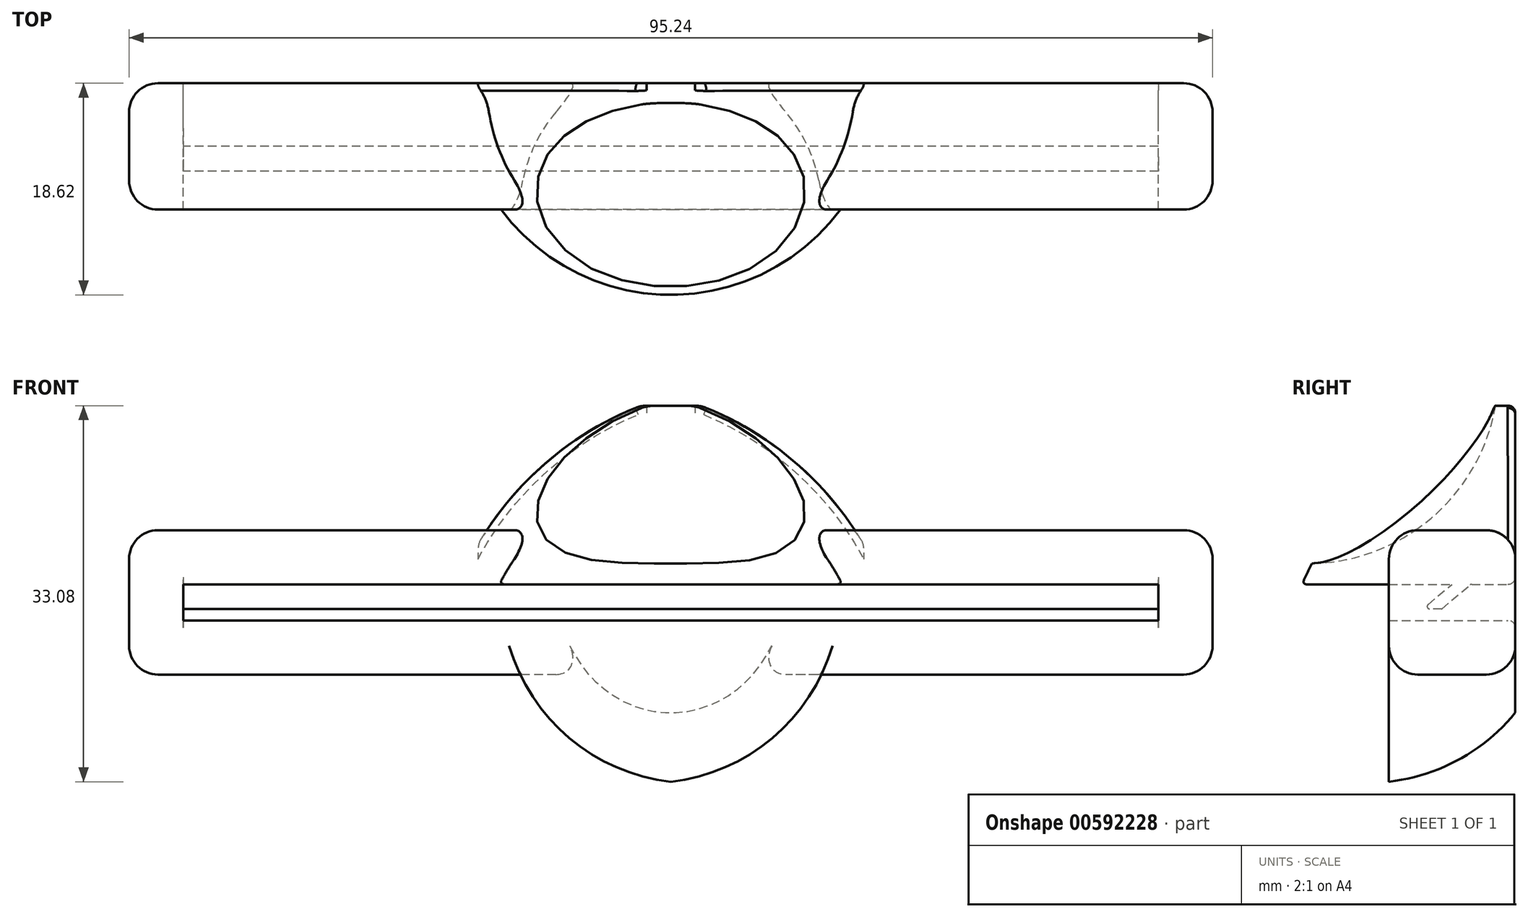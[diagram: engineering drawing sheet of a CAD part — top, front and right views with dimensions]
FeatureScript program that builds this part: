
annotation { "Feature Type Name" : "Feature", "Feature Type Description" : "" }
export const myFeature = defineFeature(function(context is Context, id is Id, definition is map)
    precondition{}
    {
        {
            var Q0;
            Q0=qCreatedBy(makeId("Front.planeOp"),FACE);
            var sketch = newSketch(context, id + "F0", { "sketchPlane" : qUnion([Q0])});
            skLineSegment(sketch, "E0.bottom", {"start": v(42.86, -1.59) * mm, "end": v(-42.86, -1.59) * mm});
            skLineSegment(sketch, "E0.top", {"start": v(42.86, 1.59) * mm, "end": v(-42.86, 1.59) * mm});
            skLineSegment(sketch, "E0.left", {"start": v(42.86, -1.59) * mm, "end": v(42.86, 1.59) * mm});
            skLineSegment(sketch, "E0.right", {"start": v(-42.86, -1.59) * mm, "end": v(-42.86, 1.59) * mm});
            skPoint(sketch, "E0.middle", {"position": v(0, 0) * mm});
            skLineSegment(sketch, "E1.0", {"start": v(47.63, 6.35) * mm, "end": v(-47.62, 6.35) * mm});
            skLineSegment(sketch, "E1.1", {"start": v(47.63, -6.35) * mm, "end": v(47.63, 6.35) * mm});
            skLineSegment(sketch, "E1.2", {"start": v(47.63, -6.35) * mm, "end": v(-47.62, -6.35) * mm});
            skLineSegment(sketch, "E1.3", {"start": v(-47.62, -6.35) * mm, "end": v(-47.62, 6.35) * mm});
            skSolve(sketch);
        }
        {
            var Q0;
            Q0 = qSketchRegion(id + "F0", true);
            extrude(context, id + "F1", {"entities" : qUnion([Q0]), "depth" : 11.1 * mm, "offsetDistance" : 25.4 * mm});
        }
        {
            var Q0;
            Q0=makeQuery(id+"F1.opExtrude","SWEPT_FACE",FACE,{"disambiguationData":[OSD([sQuery(id+"F0.wireOp",EDGE,"E0.right")])]});
            var sketch = newSketch(context, id + "F2", { "sketchPlane" : qUnion([Q0])});
            skLineSegment(sketch, "E2", {"start": v(-5.56, 1.59) * mm, "end": v(-8.12, -0.58) * mm});
            skLineSegment(sketch, "E3", {"start": v(-8.12, -0.58) * mm, "end": v(-6.48, -0.58) * mm});
            skLineSegment(sketch, "E4.0.1", {"start": v(0, 6.35) * mm, "end": v(-11.11, 6.35) * mm});
            skLineSegment(sketch, "E4.0.2", {"start": v(-11.11, 6.35) * mm, "end": v(-11.11, -6.35) * mm});
            skLineSegment(sketch, "E4.0.3", {"start": v(-11.11, -6.35) * mm, "end": v(0, -6.35) * mm});
            skLineSegment(sketch, "E5", {"start": v(-3.9, 1.59) * mm, "end": v(-6.46, -0.57) * mm});
            skPoint(sketch, "E6.visualSharp", {"position": v(-6.47, -0.58) * mm});
            skArc(sketch, "E6.filletArc", {"start": v(-6.48, -0.58) * mm, "mid": v(-6.47, -0.57) * mm, "end": v(-6.46, -0.57) * mm});
            skLineSegment(sketch, "E7", {"start": v(-5.56, 1.59) * mm, "end": v(-3.9, 1.59) * mm});
            skSolve(sketch);
        }
        {
            var Q0;
            Q0 = qSketchRegion(id + "F2", true);
            extrude(context, id + "F3", {"entities" : qUnion([Q0]), "operationType" : NewBodyOperationType.ADD, "endBound" : BoundingType.UP_TO_NEXT, "depth" : 25.4 * mm, "offsetDistance" : 25.4 * mm});
        }
        {
            var Q0;
            Q0=makeQuery(id+"F3.opExtrude","SWEPT_EDGE",EDGE,{"disambiguationData":[OSD([sQuery(id+"F0.wireOp",EDGE,"E0.top"),sQuery(id+"F0.wireOp",EDGE,"E0.right"),sQuery(id+"F2.wireOp",EDGE,"TzPzhfrO-n8Sb-AZqS-cfUP-Q4RwWiP4V3qO"),sQuery(id+"F2.wireOp",EDGE,"DA7K2Kf5-dVk4-9vVa-SaD1-1n64DXrW5RF1")])]});
            fillet(context, id + "F4", {"entities" : qUnion([Q0]), "radius" : 0.22 * mm, "tangentPropagation" : true, "allowEdgeOverflow" : false});
        }
        {
            var Q0;
            Q0=qCreatedBy(makeId("Right.planeOp"),FACE);
            var sketch = newSketch(context, id + "F5", { "sketchPlane" : qUnion([Q0])});
            skLineSegment(sketch, "E8", {"start": v(0, 1.59) * mm, "end": v(0, 17.3) * mm});
            skLineSegment(sketch, "E9.0", {"start": v(-11.11, -6.35) * mm, "end": v(-11.11, 6.35) * mm, "construction": true});
            skPoint(sketch, "E10", {"position": v(-19.34, 0) * mm});
            skPoint(sketch, "E10.positionSnap0", {"position": v(-11.11, 0) * mm});
            skArc(sketch, "E11", {"start": v(-3.2, 17.1) * mm, "mid": v(-12.37, 11) * mm, "end": v(-18.6, 1.9) * mm});
            skLineSegment(sketch, "E12.0", {"start": v(-11.11, 6.35) * mm, "end": v(0, 6.35) * mm, "construction": true});
            skLineSegment(sketch, "E13", {"start": v(-5.56, 6.35) * mm, "end": v(-5.56, 1.59) * mm});
            skLineSegment(sketch, "E14", {"start": v(-18.39, 1.59) * mm, "end": v(0, 1.59) * mm});
            skPoint(sketch, "E15.orphan", {"position": v(0, 0) * mm});
            skLineSegment(sketch, "E16", {"start": v(-2.21, 17.3) * mm, "end": v(0, 17.3) * mm});
            skPoint(sketch, "E17.visualSharp", {"position": v(-2.7, 17.3) * mm});
            skArc(sketch, "E17.filletArc", {"start": v(-2.21, 17.3) * mm, "mid": v(-2.71, 17.25) * mm, "end": v(-3.2, 17.1) * mm});
            skPoint(sketch, "E18.visualSharp", {"position": v(-18.73, 1.59) * mm});
            skArc(sketch, "E18.filletArc", {"start": v(-18.6, 1.9) * mm, "mid": v(-18.58, 1.7) * mm, "end": v(-18.39, 1.59) * mm});
            skLineSegment(sketch, "E19", {"start": v(-5.56, 1.59) * mm, "end": v(-8.57, 1.59) * mm});
            skSolve(sketch);
        }
        {
            var Q0;
            {var subQ0=sQuery(id+"F5.wireOp",EDGE,"E8");Q0=makeQuery(id+"F5.imprint","IMPRINT",FACE,{"disambiguationData":[TD([[makeQuery(id+"F5.imprint","IMPRINT",EDGE,{"derivedFrom":subQ0}),1.0]])]});}
            var Q1;
            Q1=sQuery(id+"F5.wireOp",EDGE,"E8");
            revolve(context, id + "F6", {"operationType" : NewBodyOperationType.ADD, "entities" : qUnion([Q0]), "axis" : qUnion([Q1]), "revolveType" : RevolveType.FULL});
        }
        {
            var Q0;
            Q0=makeQuery(id+"F1.opExtrude","CAP_FACE",FACE,{"disambiguationData":[OSD([sQuery(id+"F0.wireOp",EDGE,"E0.bottom"),sQuery(id+"F0.wireOp",EDGE,"E0.top"),sQuery(id+"F0.wireOp",EDGE,"E0.left"),sQuery(id+"F0.wireOp",EDGE,"E0.right"),sQuery(id+"F0.wireOp",EDGE,"E1.0"),sQuery(id+"F0.wireOp",EDGE,"E1.1"),sQuery(id+"F0.wireOp",EDGE,"E1.2"),sQuery(id+"F0.wireOp",EDGE,"E1.3")])],"isStart":true});
            var sketch = newSketch(context, id + "F7", { "sketchPlane" : qUnion([Q0])});
            skLineSegment(sketch, "E20.bottom", {"start": v(49.63, -31.38) * mm, "end": v(-49.63, -31.38) * mm});
            skLineSegment(sketch, "E20.top", {"start": v(49.63, 31.38) * mm, "end": v(-49.63, 31.38) * mm});
            skLineSegment(sketch, "E20.left", {"start": v(49.63, -31.38) * mm, "end": v(49.63, 31.38) * mm});
            skLineSegment(sketch, "E20.right", {"start": v(-49.63, -31.38) * mm, "end": v(-49.63, 31.38) * mm});
            skPoint(sketch, "E20.middle", {"position": v(0, 0) * mm});
            skSolve(sketch);
        }
        {
            var Q0;
            Q0 = qSketchRegion(id + "F7", true);
            extrude(context, id + "F8", {"entities" : qUnion([Q0]), "operationType" : NewBodyOperationType.REMOVE, "depth" : 25.4 * mm, "offsetDistance" : 25.4 * mm});
        }
        {
            var Q0;
            Q0=qCreatedBy(makeId("Right.planeOp"),FACE);
            var sketch = newSketch(context, id + "F9", { "sketchPlane" : qUnion([Q0])});
            skEllipse(sketch, "E21", {"center": v(-17.9, 19.7) * mm, "majorRadius": 16.51 * mm, "minorRadius": 16.17 * mm, "majorAxis": v(-0.8, -0.6)});
            skLineSegment(sketch, "E22", {"start": v(-35.27, 36.5) * mm, "end": v(-35.27, 1.88) * mm, "construction": true});
            skSolve(sketch);
        }
        {
            var Q0;
            Q0=makeQuery(id+"F9.imprint","IMPRINT",FACE,{"disambiguationData":[TD([[makeQuery(id+"F9.imprint","IMPRINT",EDGE,{"derivedFrom":sQuery(id+"F9.wireOp",EDGE,"E21")}),1.0]])]});
            var Q1;
            Q1=sQuery(id+"F9.wireOp",EDGE,"E22");
            revolve(context, id + "F10", {"operationType" : NewBodyOperationType.REMOVE, "entities" : qUnion([Q0]), "axis" : qUnion([Q1]), "revolveType" : RevolveType.FULL});
        }
        {
            var Q0;
            Q0=makeQuery(id+"F1.opExtrude","SWEPT_EDGE",EDGE,{"disambiguationData":[OSD([sQuery(id+"F0.wireOp",EDGE,"E1.0"),sQuery(id+"F0.wireOp",EDGE,"E1.3")])]});
            var Q1;
            Q1=makeQuery(id+"F1.opExtrude","SWEPT_EDGE",EDGE,{"disambiguationData":[OSD([sQuery(id+"F0.wireOp",EDGE,"E1.0"),sQuery(id+"F0.wireOp",EDGE,"E1.1")])]});
            var Q2;
            Q2=makeQuery(id+"F1.opExtrude","SWEPT_EDGE",EDGE,{"disambiguationData":[OSD([sQuery(id+"F0.wireOp",EDGE,"E1.1"),sQuery(id+"F0.wireOp",EDGE,"E1.2")])]});
            var Q3;
            {var subQ0=sQuery(id+"F0.wireOp",EDGE,"E1.3");var subQ1=sQuery(id+"F0.wireOp",EDGE,"E1.0");Q3=makeQuery(id+"F6.boolean.opBoolean","SPLIT",EDGE,{"disambiguationData":[TD([makeQuery(id+"F1.opExtrude","SWEPT_FACE",FACE,{"disambiguationData":[OSD([subQ0])]})])],"derivedFrom":makeQuery(id+"F1.opExtrude","CAP_EDGE",EDGE,{"disambiguationData":[OSD([subQ1])],"isStart":false})});}
            var Q4;
            Q4=makeQuery(id+"F1.opExtrude","CAP_EDGE",EDGE,{"disambiguationData":[OSD([sQuery(id+"F0.wireOp",EDGE,"E1.3")])],"isStart":false});
            var Q5;
            Q5=makeQuery(id+"F1.opExtrude","CAP_EDGE",EDGE,{"disambiguationData":[OSD([sQuery(id+"F0.wireOp",EDGE,"E1.3")])],"isStart":true});
            var Q6;
            {var subQ0=sQuery(id+"F0.wireOp",EDGE,"E1.3");var subQ1=sQuery(id+"F0.wireOp",EDGE,"E1.0");Q6=makeQuery(id+"F6.boolean.opBoolean","SPLIT",EDGE,{"disambiguationData":[TD([makeQuery(id+"F1.opExtrude","SWEPT_FACE",FACE,{"disambiguationData":[OSD([subQ0])]})])],"derivedFrom":makeQuery(id+"F1.opExtrude","CAP_EDGE",EDGE,{"disambiguationData":[OSD([subQ1])],"isStart":true})});}
            var Q7;
            {var subQ0=sQuery(id+"F0.wireOp",EDGE,"E1.1");var subQ1=sQuery(id+"F0.wireOp",EDGE,"E1.0");Q7=makeQuery(id+"F6.boolean.opBoolean","SPLIT",EDGE,{"disambiguationData":[TD([makeQuery(id+"F1.opExtrude","SWEPT_FACE",FACE,{"disambiguationData":[OSD([subQ0])]})])],"derivedFrom":makeQuery(id+"F1.opExtrude","CAP_EDGE",EDGE,{"disambiguationData":[OSD([subQ1])],"isStart":true})});}
            var Q8;
            {var subQ0=sQuery(id+"F0.wireOp",EDGE,"E1.1");var subQ1=sQuery(id+"F0.wireOp",EDGE,"E1.0");Q8=makeQuery(id+"F6.boolean.opBoolean","SPLIT",EDGE,{"disambiguationData":[TD([makeQuery(id+"F1.opExtrude","SWEPT_FACE",FACE,{"disambiguationData":[OSD([subQ0])]})])],"derivedFrom":makeQuery(id+"F1.opExtrude","CAP_EDGE",EDGE,{"disambiguationData":[OSD([subQ1])],"isStart":false})});}
            var Q9;
            Q9=makeQuery(id+"F1.opExtrude","CAP_EDGE",EDGE,{"disambiguationData":[OSD([sQuery(id+"F0.wireOp",EDGE,"E1.1")])],"isStart":true});
            var Q10;
            Q10=makeQuery(id+"F1.opExtrude","CAP_EDGE",EDGE,{"disambiguationData":[OSD([sQuery(id+"F0.wireOp",EDGE,"E1.1")])],"isStart":false});
            var Q11;
            Q11=makeQuery(id+"F1.opExtrude","SWEPT_FACE",FACE,{"disambiguationData":[OSD([sQuery(id+"F0.wireOp",EDGE,"E1.3")])]});
            fillet(context, id + "F11", {"entities" : qUnion([Q0, Q1, Q2, Q3, Q4, Q5, Q6, Q7, Q8, Q9, Q10, Q11]), "radius" : 2.54 * mm, "tangentPropagation" : true, "allowEdgeOverflow" : false});
        }
        {
            var Q0;
            Q0=makeQuery(id+"F8.boolean.opBoolean","INTERSECT",EDGE,{"disambiguationData":[OD(3.0)],"derivedFrom":[makeQuery(id+"F6.opRevolve","SWEPT_FACE",FACE,{"disambiguationData":[OSD([sQuery(id+"F5.wireOp",EDGE,"E11")])]}),makeQuery(id+"F8.opExtrude","CAP_FACE",FACE,{"disambiguationData":[OSD([sQuery(id+"F7.wireOp",EDGE,"E20.bottom"),sQuery(id+"F7.wireOp",EDGE,"E20.top"),sQuery(id+"F7.wireOp",EDGE,"E20.left"),sQuery(id+"F7.wireOp",EDGE,"E20.right")])],"isStart":true})]});
            var Q1;
            Q1=makeQuery(id+"F8.boolean.opBoolean","INTERSECT",EDGE,{"disambiguationData":[OD(0.0)],"derivedFrom":[makeQuery(id+"F6.opRevolve","SWEPT_FACE",FACE,{"disambiguationData":[OSD([sQuery(id+"F5.wireOp",EDGE,"NLCN7o5y-JNbc-YAga-TzhH-OMJWU77clgbR")])]}),makeQuery(id+"F8.opExtrude","CAP_FACE",FACE,{"disambiguationData":[OSD([sQuery(id+"F7.wireOp",EDGE,"E20.bottom"),sQuery(id+"F7.wireOp",EDGE,"E20.top"),sQuery(id+"F7.wireOp",EDGE,"E20.left"),sQuery(id+"F7.wireOp",EDGE,"E20.right")])],"isStart":true})]});
            var Q2;
            Q2=makeQuery(id+"F8.boolean.opBoolean","INTERSECT",EDGE,{"disambiguationData":[OD(1.0)],"derivedFrom":[makeQuery(id+"F6.opRevolve","SWEPT_FACE",FACE,{"disambiguationData":[OSD([sQuery(id+"F5.wireOp",EDGE,"NLCN7o5y-JNbc-YAga-TzhH-OMJWU77clgbR")])]}),makeQuery(id+"F8.opExtrude","CAP_FACE",FACE,{"disambiguationData":[OSD([sQuery(id+"F7.wireOp",EDGE,"E20.bottom"),sQuery(id+"F7.wireOp",EDGE,"E20.top"),sQuery(id+"F7.wireOp",EDGE,"E20.left"),sQuery(id+"F7.wireOp",EDGE,"E20.right")])],"isStart":true})]});
            var Q3;
            Q3=makeQuery(id+"F8.boolean.opBoolean","INTERSECT",EDGE,{"disambiguationData":[OD(1.0)],"derivedFrom":[makeQuery(id+"F6.opRevolve","SWEPT_FACE",FACE,{"disambiguationData":[OSD([sQuery(id+"F5.wireOp",EDGE,"e4f496ee-d8f1-49a1-bda9-2c2582ce3000.filletArc")])]}),makeQuery(id+"F8.opExtrude","CAP_FACE",FACE,{"disambiguationData":[OSD([sQuery(id+"F7.wireOp",EDGE,"E20.bottom"),sQuery(id+"F7.wireOp",EDGE,"E20.top"),sQuery(id+"F7.wireOp",EDGE,"E20.left"),sQuery(id+"F7.wireOp",EDGE,"E20.right")])],"isStart":true})]});
            var Q4;
            Q4=makeQuery(id+"F8.boolean.opBoolean","INTERSECT",EDGE,{"disambiguationData":[OD(0.0)],"derivedFrom":[makeQuery(id+"F6.opRevolve","SWEPT_FACE",FACE,{"disambiguationData":[OSD([sQuery(id+"F5.wireOp",EDGE,"e4f496ee-d8f1-49a1-bda9-2c2582ce3000.filletArc")])]}),makeQuery(id+"F8.opExtrude","CAP_FACE",FACE,{"disambiguationData":[OSD([sQuery(id+"F7.wireOp",EDGE,"E20.bottom"),sQuery(id+"F7.wireOp",EDGE,"E20.top"),sQuery(id+"F7.wireOp",EDGE,"E20.left"),sQuery(id+"F7.wireOp",EDGE,"E20.right")])],"isStart":true})]});
            var Q5;
            Q5=makeQuery(id+"F8.boolean.opBoolean","INTERSECT",EDGE,{"disambiguationData":[OD(2.0)],"derivedFrom":[makeQuery(id+"F6.opRevolve","SWEPT_FACE",FACE,{"disambiguationData":[OSD([sQuery(id+"F5.wireOp",EDGE,"E11")])]}),makeQuery(id+"F8.opExtrude","CAP_FACE",FACE,{"disambiguationData":[OSD([sQuery(id+"F7.wireOp",EDGE,"E20.bottom"),sQuery(id+"F7.wireOp",EDGE,"E20.top"),sQuery(id+"F7.wireOp",EDGE,"E20.left"),sQuery(id+"F7.wireOp",EDGE,"E20.right")])],"isStart":true})]});
            fillet(context, id + "F12", {"entities" : qUnion([Q0, Q1, Q2, Q3, Q4, Q5]), "radius" : 0.64 * mm, "tangentPropagation" : true, "allowEdgeOverflow" : false});
        }
        {
            var Q0;
            Q0=qCreatedBy(makeId("Right.planeOp"),FACE);
            var sketch = newSketch(context, id + "F13", { "sketchPlane" : qUnion([Q0])});
            skLineSegment(sketch, "E23.0", {"start": v(-9.84, -6.35) * mm, "end": v(-1.27, -6.35) * mm});
            skLineSegment(sketch, "E24.0.1", {"start": v(-2.54, 3.8) * mm, "end": v(-2.54, -5.08) * mm});
            skLineSegment(sketch, "E24.0.2", {"start": v(-2.54, 3.8) * mm, "end": v(0, 3.8) * mm});
            skLineSegment(sketch, "E24.0.3", {"start": v(0, 3.8) * mm, "end": v(0, -5.08) * mm, "construction": true});
            skLineSegment(sketch, "E25.0.1", {"start": v(-2.54, 3.8) * mm, "end": v(-2.54, -5.08) * mm, "construction": true});
            skLineSegment(sketch, "E25.0.2", {"start": v(-2.54, 3.8) * mm, "end": v(0, 3.8) * mm, "construction": true});
            skLineSegment(sketch, "E26", {"start": v(0, -6.35) * mm, "end": v(-11.11, -6.35) * mm});
            skLineSegment(sketch, "E27", {"start": v(0, -6.35) * mm, "end": v(2.14, -6.35) * mm});
            skLineSegment(sketch, "E28", {"start": v(-11.11, -6.35) * mm, "end": v(-11.11, -15.78) * mm});
            skArc(sketch, "E29", {"start": v(-11.11, -15.78) * mm, "mid": v(-3.27, -12.77) * mm, "end": v(2.14, -6.35) * mm});
            skPoint(sketch, "E30.0.start.orphan", {"position": v(-11.11, 3.8) * mm});
            skSolve(sketch);
        }
        {
            var Q0;
            {var subQ0=sQuery(id+"F13.wireOp",EDGE,"E27");Q0=makeQuery(id+"F13.imprint","IMPRINT",FACE,{"disambiguationData":[TD([[makeQuery(id+"F13.imprint","IMPRINT",EDGE,{"derivedFrom":subQ0}),-1.0]])]});}
            var Q1;
            Q1=sQuery(id+"F13.wireOp",EDGE,"E28");
            revolve(context, id + "F14", {"operationType" : NewBodyOperationType.ADD, "entities" : qUnion([Q0]), "axis" : qUnion([Q1]), "revolveType" : RevolveType.FULL});
        }
        {
            var Q0;
            Q0=qCreatedBy(makeId("Top.planeOp"),FACE);
            var sketch = newSketch(context, id + "F15", { "sketchPlane" : qUnion([Q0])});
            skLineSegment(sketch, "E31.0", {"start": v(-13.25, -11.11) * mm, "end": v(-45.09, -11.11) * mm, "construction": true});
            skLineSegment(sketch, "E32.0", {"start": v(-7.21, 0) * mm, "end": v(-45.09, 0) * mm, "construction": true});
            skLineSegment(sketch, "E33.bottom", {"start": v(-17.93, -11.11) * mm, "end": v(17.64, -11.11) * mm});
            skLineSegment(sketch, "E33.top", {"start": v(-17.93, -26.95) * mm, "end": v(17.64, -26.95) * mm});
            skLineSegment(sketch, "E33.left", {"start": v(-17.93, -11.11) * mm, "end": v(-17.93, -26.95) * mm});
            skLineSegment(sketch, "E33.right", {"start": v(17.64, -11.11) * mm, "end": v(17.64, -26.95) * mm});
            skLineSegment(sketch, "E34.bottom", {"start": v(-17.4, 0) * mm, "end": v(17.73, 0) * mm});
            skLineSegment(sketch, "E34.top", {"start": v(-17.4, 13.15) * mm, "end": v(17.73, 13.15) * mm});
            skLineSegment(sketch, "E34.left", {"start": v(-17.4, 0) * mm, "end": v(-17.4, 13.15) * mm});
            skLineSegment(sketch, "E34.right", {"start": v(17.73, 0) * mm, "end": v(17.73, 13.15) * mm});
            skSolve(sketch);
        }
        {
            var Q0;
            Q0=makeQuery(id+"F15.imprint","IMPRINT",FACE,{"disambiguationData":[TD([[makeQuery(id+"F15.imprint","IMPRINT",EDGE,{"derivedFrom":sQuery(id+"F15.wireOp",EDGE,"E33.bottom")}),-1.0]])]});
            var Q1;
            Q1=makeQuery(id+"F15.imprint","IMPRINT",FACE,{"disambiguationData":[TD([[makeQuery(id+"F15.imprint","IMPRINT",EDGE,{"derivedFrom":sQuery(id+"F15.wireOp",EDGE,"E34.bottom")}),1.0]])]});
            extrude(context, id + "F16", {"entities" : qUnion([Q0, Q1]), "operationType" : NewBodyOperationType.REMOVE, "oppositeDirection" : true, "depth" : 25.4 * mm, "offsetDistance" : 25.4 * mm});
        }
        {
            var Q0;
            {var subQ0=sQuery(id+"F0.wireOp",EDGE,"E1.3");var subQ1=sQuery(id+"F0.wireOp",EDGE,"E1.2");var subQ2=makeQuery(id+"F1.opExtrude","SWEPT_FACE",FACE,{"disambiguationData":[OSD([subQ1])]});var subQ3=makeQuery(id+"F1.opExtrude","CAP_FACE",FACE,{"disambiguationData":[OSD([sQuery(id+"F0.wireOp",EDGE,"E0.bottom"),sQuery(id+"F0.wireOp",EDGE,"E0.top"),sQuery(id+"F0.wireOp",EDGE,"E0.left"),sQuery(id+"F0.wireOp",EDGE,"E0.right"),sQuery(id+"F0.wireOp",EDGE,"E1.0"),sQuery(id+"F0.wireOp",EDGE,"E1.1"),subQ1,subQ0])],"isStart":false});Q0=makeQuery(id+"F14.boolean.opBoolean","SPLIT",EDGE,{"disambiguationData":[topologyDisambiguationEdgeConnected([subQ3,subQ2]),TD([makeQuery(id+"F11.opFillet","BLEND_FACE",FACE,{"disambiguationData":[OSD([subQ0]),TDD([makeQuery(id+"F1.opExtrude","CAP_EDGE",EDGE,{"disambiguationData":[OSD([subQ0])],"isStart":false})])]})])],"derivedFrom":makeQuery(id+"F1.opExtrude","CAP_EDGE",EDGE,{"disambiguationData":[OSD([subQ1])],"isStart":false})});}
            var Q1;
            {var subQ0=makeQuery(id+"F8.opExtrude","CAP_FACE",FACE,{"disambiguationData":[OSD([sQuery(id+"F7.wireOp",EDGE,"E20.bottom"),sQuery(id+"F7.wireOp",EDGE,"E20.top"),sQuery(id+"F7.wireOp",EDGE,"E20.left"),sQuery(id+"F7.wireOp",EDGE,"E20.right")])],"isStart":true});var subQ1=sQuery(id+"F0.wireOp",EDGE,"E1.3");var subQ2=sQuery(id+"F0.wireOp",EDGE,"E1.2");var subQ3=makeQuery(id+"F1.opExtrude","SWEPT_FACE",FACE,{"disambiguationData":[OSD([subQ2])]});var subQ4=makeQuery(id+"F1.opExtrude","CAP_FACE",FACE,{"disambiguationData":[OSD([sQuery(id+"F0.wireOp",EDGE,"E0.bottom"),sQuery(id+"F0.wireOp",EDGE,"E0.top"),sQuery(id+"F0.wireOp",EDGE,"E0.left"),sQuery(id+"F0.wireOp",EDGE,"E0.right"),sQuery(id+"F0.wireOp",EDGE,"E1.0"),sQuery(id+"F0.wireOp",EDGE,"E1.1"),subQ2,subQ1])],"isStart":true});Q1=makeQuery(id+"F14.boolean.opBoolean","SPLIT",EDGE,{"disambiguationData":[topologyDisambiguationEdgeConnected([subQ4,subQ3,subQ0]),TD([makeQuery(id+"F11.opFillet","BLEND_FACE",FACE,{"disambiguationData":[OSD([subQ1]),TDD([makeQuery(id+"F1.opExtrude","CAP_EDGE",EDGE,{"disambiguationData":[OSD([subQ1])],"isStart":true})])]})])],"derivedFrom":makeQuery(id+"F1.opExtrude","CAP_EDGE",EDGE,{"disambiguationData":[OSD([subQ2])],"isStart":true})});}
            var Q2;
            {var subQ0=sQuery(id+"F0.wireOp",EDGE,"E1.2");var subQ1=sQuery(id+"F0.wireOp",EDGE,"E1.1");var subQ2=makeQuery(id+"F8.opExtrude","CAP_FACE",FACE,{"disambiguationData":[OSD([sQuery(id+"F7.wireOp",EDGE,"E20.bottom"),sQuery(id+"F7.wireOp",EDGE,"E20.top"),sQuery(id+"F7.wireOp",EDGE,"E20.left"),sQuery(id+"F7.wireOp",EDGE,"E20.right")])],"isStart":true});var subQ3=makeQuery(id+"F1.opExtrude","SWEPT_FACE",FACE,{"disambiguationData":[OSD([subQ0])]});var subQ4=makeQuery(id+"F1.opExtrude","CAP_FACE",FACE,{"disambiguationData":[OSD([sQuery(id+"F0.wireOp",EDGE,"E0.bottom"),sQuery(id+"F0.wireOp",EDGE,"E0.top"),sQuery(id+"F0.wireOp",EDGE,"E0.left"),sQuery(id+"F0.wireOp",EDGE,"E0.right"),sQuery(id+"F0.wireOp",EDGE,"E1.0"),subQ1,subQ0,sQuery(id+"F0.wireOp",EDGE,"E1.3")])],"isStart":true});Q2=makeQuery(id+"F14.boolean.opBoolean","SPLIT",EDGE,{"disambiguationData":[topologyDisambiguationEdgeConnected([subQ4,subQ3,subQ2]),TD([makeQuery(id+"F11.opFillet","BLEND_FACE",FACE,{"disambiguationData":[OSD([subQ1]),TDD([makeQuery(id+"F1.opExtrude","CAP_EDGE",EDGE,{"disambiguationData":[OSD([subQ1])],"isStart":true})])]})])],"derivedFrom":makeQuery(id+"F1.opExtrude","CAP_EDGE",EDGE,{"disambiguationData":[OSD([subQ0])],"isStart":true})});}
            var Q3;
            {var subQ0=sQuery(id+"F0.wireOp",EDGE,"E1.2");var subQ1=sQuery(id+"F0.wireOp",EDGE,"E1.1");var subQ2=makeQuery(id+"F1.opExtrude","SWEPT_FACE",FACE,{"disambiguationData":[OSD([subQ0])]});var subQ3=makeQuery(id+"F1.opExtrude","CAP_FACE",FACE,{"disambiguationData":[OSD([sQuery(id+"F0.wireOp",EDGE,"E0.bottom"),sQuery(id+"F0.wireOp",EDGE,"E0.top"),sQuery(id+"F0.wireOp",EDGE,"E0.left"),sQuery(id+"F0.wireOp",EDGE,"E0.right"),sQuery(id+"F0.wireOp",EDGE,"E1.0"),subQ1,subQ0,sQuery(id+"F0.wireOp",EDGE,"E1.3")])],"isStart":false});Q3=makeQuery(id+"F14.boolean.opBoolean","SPLIT",EDGE,{"disambiguationData":[topologyDisambiguationEdgeConnected([subQ3,subQ2]),TD([makeQuery(id+"F11.opFillet","BLEND_FACE",FACE,{"disambiguationData":[OSD([subQ1]),TDD([makeQuery(id+"F1.opExtrude","CAP_EDGE",EDGE,{"disambiguationData":[OSD([subQ1])],"isStart":false})])]})])],"derivedFrom":makeQuery(id+"F1.opExtrude","CAP_EDGE",EDGE,{"disambiguationData":[OSD([subQ0])],"isStart":false})});}
            fillet(context, id + "F17", {"entities" : qUnion([Q0, Q1, Q2, Q3]), "radius" : 2.54 * mm, "tangentPropagation" : true, "allowEdgeOverflow" : false});
        }
        {
            var Q0;
            {var subQ1=sQuery(id+"F0.wireOp",EDGE,"E0.right");var subQ2=sQuery(id+"F0.wireOp",EDGE,"E0.top");var subQ4=sQuery(id+"F0.wireOp",EDGE,"E0.left");var subQ7=makeQuery(id+"F1.opExtrude","CAP_EDGE",EDGE,{"disambiguationData":[OSD([subQ2])],"isStart":true});Q0=makeQuery(id+"F8.boolean.opBoolean","MERGE",EDGE,{"derivedFrom":[makeQuery(id+"F6.boolean.opBoolean","SPLIT",EDGE,{"disambiguationData":[TD([makeQuery(id+"F1.opExtrude","SWEPT_FACE",FACE,{"disambiguationData":[OSD([subQ4])]})])],"derivedFrom":subQ7}),makeQuery(id+"F6.boolean.opBoolean","SPLIT",EDGE,{"disambiguationData":[TD([makeQuery(id+"F1.opExtrude","SWEPT_FACE",FACE,{"disambiguationData":[OSD([subQ1])]})])],"derivedFrom":subQ7})]});}
            var Q1;
            Q1=makeQuery(id+"F1.opExtrude","CAP_EDGE",EDGE,{"disambiguationData":[OSD([sQuery(id+"F0.wireOp",EDGE,"E0.bottom")])],"isStart":true});
            fillet(context, id + "F18", {"entities" : qUnion([Q0, Q1]), "radius" : 0.64 * mm, "tangentPropagation" : true, "allowEdgeOverflow" : false});
        }
        {
            var Q0;
            Q0=makeQuery(id+"F3.opExtrude","SWEPT_EDGE",EDGE,{"disambiguationData":[OSD([sQuery(id+"F2.wireOp",EDGE,"E2"),sQuery(id+"F2.wireOp",EDGE,"E3")])]});
            fillet(context, id + "F19", {"entities" : qUnion([Q0]), "radius" : 0.22 * mm, "tangentPropagation" : true, "allowEdgeOverflow" : false});
        }
    });
